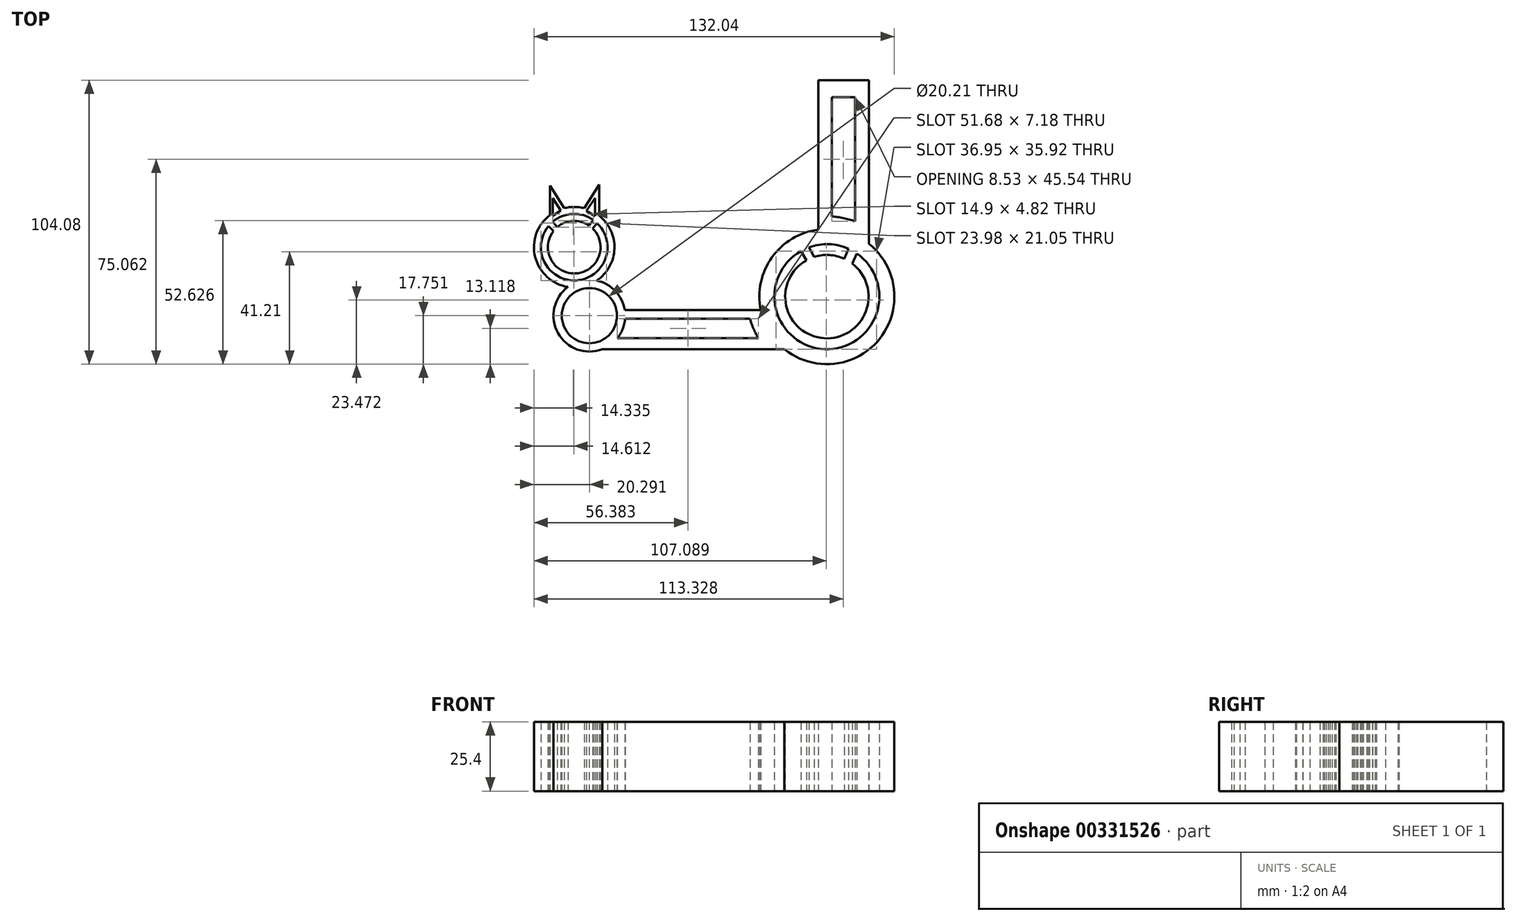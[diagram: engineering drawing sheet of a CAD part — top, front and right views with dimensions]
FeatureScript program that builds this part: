
annotation { "Feature Type Name" : "Feature", "Feature Type Description" : "" }
export const myFeature = defineFeature(function(context is Context, id is Id, definition is map)
    precondition{}
    {
        {
            var Q0;
            Q0=qCreatedBy(makeId("Top.planeOp"),FACE);
            var sketch = newSketch(context, id + "F0", { "sketchPlane" : qUnion([Q0])});
            skArc(sketch, "E0", {"start": v(29.83, -6.33) * mm, "mid": v(38.56, -42.25) * mm, "end": v(50.32, -7.2) * mm});
            skLineSegment(sketch, "E1", {"start": v(15.2, -27.95) * mm, "end": v(-34.66, -27.95) * mm});
            skLineSegment(sketch, "E2", {"start": v(23.95, -42.28) * mm, "end": v(-43.22, -42.28) * mm});
            skArc(sketch, "E3", {"start": v(11.16, -31.05) * mm, "mid": v(12.49, -34.75) * mm, "end": v(14.3, -38.23) * mm});
            skLineSegment(sketch, "E4", {"start": v(14.3, -38.23) * mm, "end": v(-37.39, -38.23) * mm});
            skArc(sketch, "E5", {"start": v(-34.66, -27.95) * mm, "mid": v(-38.12, -20.94) * mm, "end": v(-44.95, -17.14) * mm});
            skLineSegment(sketch, "E6", {"start": v(11.16, -31.05) * mm, "end": v(-34.54, -31.05) * mm});
            skLineSegment(sketch, "E7", {"start": v(36.22, 1.44) * mm, "end": v(36.22, 56.32) * mm});
            skLineSegment(sketch, "E8", {"start": v(36.22, 56.32) * mm, "end": v(54.76, 56.32) * mm});
            skLineSegment(sketch, "E9", {"start": v(54.76, 56.32) * mm, "end": v(54.76, -3.73) * mm});
            skArc(sketch, "E10", {"start": v(11.08, -31.05) * mm, "mid": v(12.4, -34.75) * mm, "end": v(14.2, -38.23) * mm});
            skArc(sketch, "E11.trimOffspring", {"start": v(49.66, 4.53) * mm, "mid": v(45.47, 5.75) * mm, "end": v(41.13, 6.34) * mm});
            skArc(sketch, "E12", {"start": v(36.22, 1.5) * mm, "mid": v(19.26, -8.64) * mm, "end": v(15.14, -27.95) * mm});
            skLineSegment(sketch, "E13", {"start": v(41.13, 6.34) * mm, "end": v(41.13, 50.07) * mm});
            skLineSegment(sketch, "E14", {"start": v(41.13, 50.07) * mm, "end": v(49.66, 50.07) * mm});
            skLineSegment(sketch, "E15", {"start": v(49.66, 50.07) * mm, "end": v(49.66, 4.53) * mm});
            skArc(sketch, "E16.trimOffspring", {"start": v(23.85, -42.28) * mm, "mid": v(58.7, -38.48) * mm, "end": v(54.76, -3.66) * mm});
            skCircle(sketch, "E17", {"center": v(-47.64, -30) * mm, "radius": 10.1 * mm});
            skArc(sketch, "E18.trimOffspring", {"start": v(-37.39, -38.23) * mm, "mid": v(-35.42, -34.86) * mm, "end": v(-34.54, -31.05) * mm});
            skArc(sketch, "E19", {"start": v(-44.95, -17.14) * mm, "mid": v(-38.45, -5.49) * mm, "end": v(-44.02, 6.64) * mm});
            skArc(sketch, "E20", {"start": v(-62.6, 2.85) * mm, "mid": v(-52.41, -17.08) * mm, "end": v(-44.83, 3.98) * mm});
            skArc(sketch, "E21.trimOffspring", {"start": v(-55.5, -19.47) * mm, "mid": v(-59.15, -36.35) * mm, "end": v(-42.93, -42.28) * mm});
            skLineSegment(sketch, "E22", {"start": v(-62.09, 6.85) * mm, "end": v(-62.09, 17.7) * mm});
            skLineSegment(sketch, "E23", {"start": v(-62.09, 17.7) * mm, "end": v(-56.86, 9.38) * mm});
            skLineSegment(sketch, "E24", {"start": v(-44.02, 6.64) * mm, "end": v(-44.02, 18.07) * mm});
            skLineSegment(sketch, "E25", {"start": v(-44.02, 18.07) * mm, "end": v(-49.52, 9.38) * mm});
            skArc(sketch, "E26.trimOffspring", {"start": v(-62.09, 6.85) * mm, "mid": v(-67.5, -8.49) * mm, "end": v(-55.5, -19.47) * mm});
            skArc(sketch, "E27.trimOffspring", {"start": v(-49.52, 9.38) * mm, "mid": v(-53.19, 9.84) * mm, "end": v(-56.86, 9.38) * mm});
            skLineSegment(sketch, "E28", {"start": v(-61.1, 13.14) * mm, "end": v(-61.1, 6.62) * mm});
            skLineSegment(sketch, "E29", {"start": v(-61.1, 6.62) * mm, "end": v(-58.08, 8.5) * mm});
            skLineSegment(sketch, "E30", {"start": v(-58.08, 8.5) * mm, "end": v(-61.1, 13.14) * mm});
            skLineSegment(sketch, "E31", {"start": v(-45.55, 13.14) * mm, "end": v(-45.55, 6.46) * mm});
            skLineSegment(sketch, "E32", {"start": v(-45.55, 6.46) * mm, "end": v(-48.77, 8.39) * mm});
            skLineSegment(sketch, "E33", {"start": v(-48.77, 8.39) * mm, "end": v(-45.55, 13.14) * mm});
            skArc(sketch, "E34", {"start": v(-60.8, 1) * mm, "mid": v(-52.56, -14.52) * mm, "end": v(-46.4, 1.93) * mm});
            skLineSegment(sketch, "E35", {"start": v(-61.04, 4.42) * mm, "end": v(-59.4, 2.46) * mm});
            skLineSegment(sketch, "E36", {"start": v(-62.6, 2.85) * mm, "end": v(-60.8, 1) * mm});
            skLineSegment(sketch, "E37", {"start": v(-46.15, 5.05) * mm, "end": v(-47.7, 3.01) * mm});
            skLineSegment(sketch, "E38", {"start": v(-44.83, 3.98) * mm, "end": v(-46.4, 1.93) * mm});
            skArc(sketch, "E39.trimOffspring", {"start": v(-46.15, 5.05) * mm, "mid": v(-53.7, 7.28) * mm, "end": v(-61.04, 4.42) * mm});
            skArc(sketch, "E40.trimOffspring", {"start": v(-47.7, 3.01) * mm, "mid": v(-53.64, 4.72) * mm, "end": v(-59.4, 2.46) * mm});
            skArc(sketch, "E41", {"start": v(31.89, -9.72) * mm, "mid": v(38.32, -38.27) * mm, "end": v(48.63, -10.88) * mm});
            skLineSegment(sketch, "E42", {"start": v(29.83, -6.33) * mm, "end": v(31.89, -9.72) * mm});
            skLineSegment(sketch, "E43", {"start": v(32.83, -4.94) * mm, "end": v(34.7, -8.49) * mm});
            skLineSegment(sketch, "E44", {"start": v(47.33, -5.51) * mm, "end": v(45.75, -9.15) * mm});
            skLineSegment(sketch, "E45", {"start": v(50.32, -7.2) * mm, "end": v(48.63, -10.88) * mm});
            skArc(sketch, "E46.trimOffspring", {"start": v(47.33, -5.51) * mm, "mid": v(40.14, -3.8) * mm, "end": v(32.83, -4.94) * mm});
            skArc(sketch, "E47.trimOffspring", {"start": v(45.75, -9.15) * mm, "mid": v(40.29, -7.78) * mm, "end": v(34.7, -8.49) * mm});
            skLineSegment(sketch, "E48", {"start": v(0, 65.07) * mm, "end": v(0, -68.73) * mm});
            skSolve(sketch);
        }
        {
            var Q0;
            Q0 = qSketchRegion(id + "F0", true);
            extrude(context, id + "F1", {"entities" : qUnion([Q0]), "depth" : 25.4 * mm});
        }
    });
